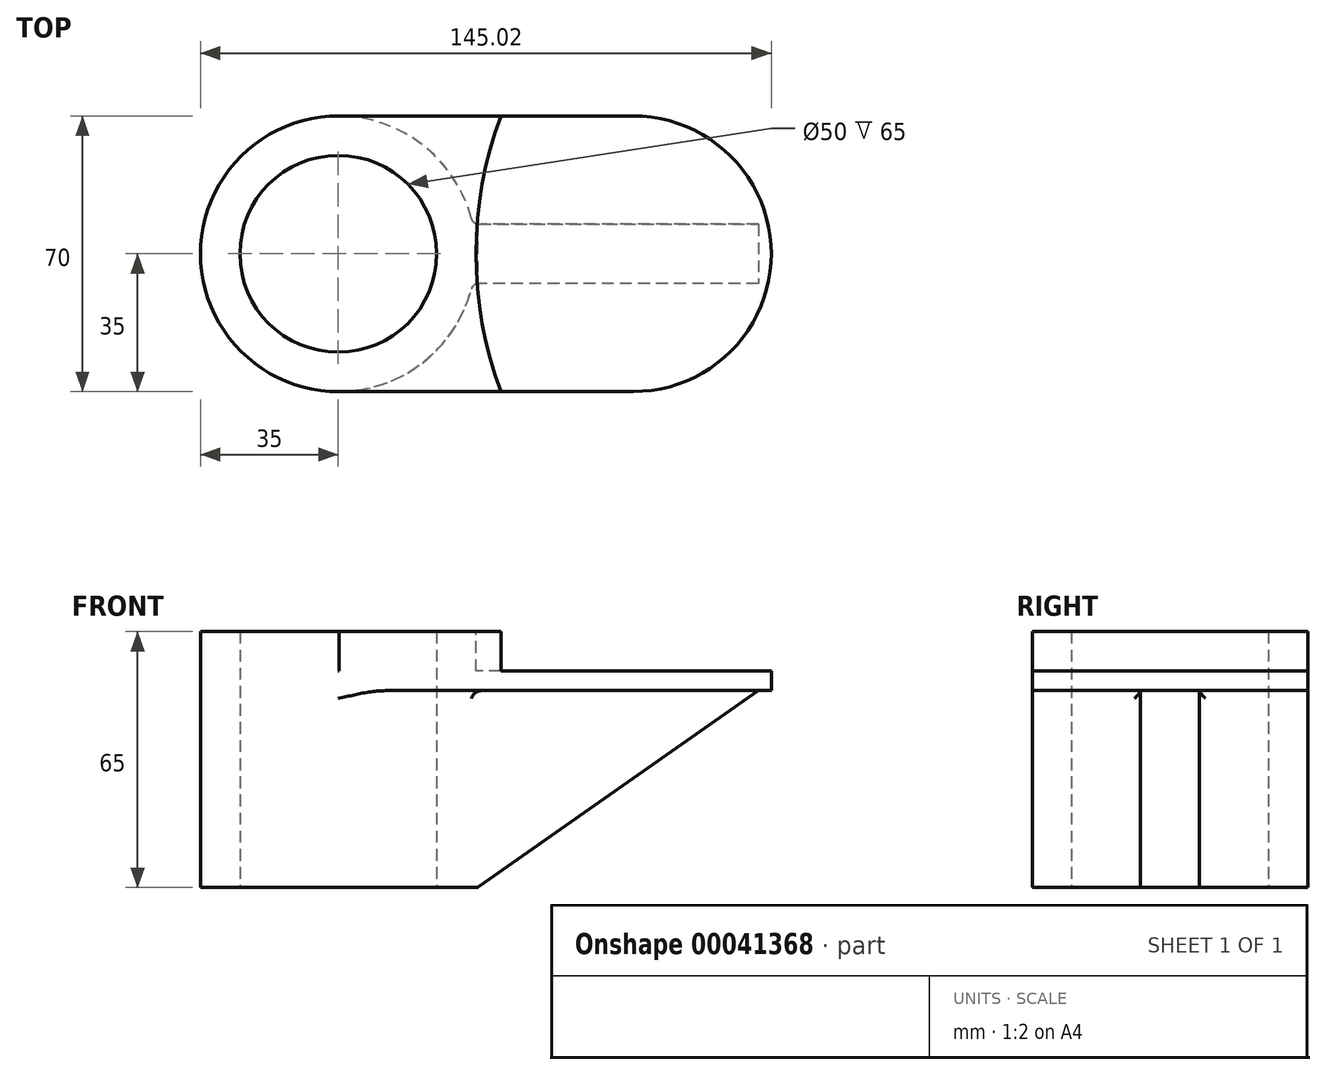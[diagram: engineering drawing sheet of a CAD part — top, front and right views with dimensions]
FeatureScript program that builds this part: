
annotation { "Feature Type Name" : "Feature", "Feature Type Description" : "" }
export const myFeature = defineFeature(function(context is Context, id is Id, definition is map)
    precondition{}
    {
        {
            var Q0;
            Q0=qCreatedBy(makeId("Top.planeOp"),FACE);
            var sketch = newSketch(context, id + "F0", { "sketchPlane" : qUnion([Q0])});
            skCircle(sketch, "E0", {"center": v(0, 0) * mm, "radius": 35 * mm});
            skSolve(sketch);
        }
        {
            var Q0;
            Q0=makeQuery(id+"F0.imprint","IMPRINT",FACE,{"disambiguationData":[TD([[makeQuery(id+"F0.imprint","IMPRINT",EDGE,{"derivedFrom":sQuery(id+"F0.wireOp",EDGE,"E0")}),1.0]])]});
            extrude(context, id + "F1", {"entities" : qUnion([Q0]), "depth" : 15 * mm, "hasSecondDirection" : true, "secondDirectionOppositeDirection" : true, "secondDirectionDepth" : 50 * mm});
        }
        {
            var Q0;
            Q0=qCreatedBy(makeId("Top.planeOp"),FACE);
            var sketch = newSketch(context, id + "F2", { "sketchPlane" : qUnion([Q0])});
            skLineSegment(sketch, "E1.rect.bottom", {"start": v(75, 35) * mm, "end": v(0, 35) * mm});
            skLineSegment(sketch, "E1.rect.top", {"start": v(75, -35) * mm, "end": v(0, -35) * mm});
            skLineSegment(sketch, "E1.rect.left", {"start": v(75, 35) * mm, "end": v(75, -35) * mm});
            skLineSegment(sketch, "E1.rect.right", {"start": v(0, 35) * mm, "end": v(0, -35) * mm});
            skPoint(sketch, "E1.rect.middle", {"position": v(37.5, 0) * mm});
            skSolve(sketch);
        }
        {
            var Q0;
            Q0=qCreatedBy(makeId("Top.planeOp"),FACE);
            var sketch = newSketch(context, id + "F3", { "sketchPlane" : qUnion([Q0])});
            skCircle(sketch, "E2", {"center": v(75.02, 0) * mm, "radius": 35 * mm});
            skSolve(sketch);
        }
        {
            var Q0;
            Q0=makeQuery(id+"F3.imprint","IMPRINT",FACE,{"disambiguationData":[TD([[makeQuery(id+"F3.imprint","IMPRINT",EDGE,{"derivedFrom":sQuery(id+"F3.wireOp",EDGE,"E2")}),1.0]])]});
            var Q1;
            Q1=makeQuery(id+"F2.imprint","IMPRINT",FACE,{"disambiguationData":[TD([[makeQuery(id+"F2.imprint","IMPRINT",EDGE,{"derivedFrom":sQuery(id+"F2.wireOp",EDGE,"E1.rect.bottom")}),1.0]])]});
            extrude(context, id + "F4", {"entities" : qUnion([Q0, Q1]), "operationType" : NewBodyOperationType.ADD, "depth" : 5 * mm});
        }
        {
            var Q0;
            Q0=makeQuery(id+"F4.boolean.opBoolean","MERGE",FACE,{"derivedFrom":[makeQuery(id+"F4.opExtrude","CAP_FACE",FACE,{"disambiguationData":[OSD([sQuery(id+"F2.wireOp",EDGE,"E1.rect.bottom"),sQuery(id+"F2.wireOp",EDGE,"E1.rect.top"),sQuery(id+"F2.wireOp",EDGE,"E1.rect.left"),sQuery(id+"F2.wireOp",EDGE,"E1.rect.right")])],"isStart":false}),makeQuery(id+"F4.opExtrude","CAP_FACE",FACE,{"disambiguationData":[OSD([sQuery(id+"F3.wireOp",EDGE,"E2")])],"isStart":false})]});
            var sketch = newSketch(context, id + "F5", { "sketchPlane" : qUnion([Q0])});
            skLineSegment(sketch, "E3.rect.bottom", {"start": v(57.08, -35) * mm, "end": v(0.17, -35) * mm});
            skLineSegment(sketch, "E3.rect.top", {"start": v(57.08, 35) * mm, "end": v(0.17, 35) * mm});
            skLineSegment(sketch, "E3.rect.left", {"start": v(57.08, -35) * mm, "end": v(57.08, 35) * mm});
            skLineSegment(sketch, "E3.rect.right", {"start": v(0.17, -35) * mm, "end": v(0.17, 35) * mm});
            skPoint(sketch, "E3.rect.middle", {"position": v(28.62, 0) * mm});
            skSolve(sketch);
        }
        {
            var Q0;
            Q0 = qSketchRegion(id + "F5", true);
            extrude(context, id + "F6", {"entities" : qUnion([Q0]), "operationType" : NewBodyOperationType.ADD, "depth" : 10 * mm});
        }
        {
            var Q0;
            Q0=makeQuery(id+"F6.boolean.opBoolean","MERGE",FACE,{"derivedFrom":[makeQuery(id+"F1.opExtrude","CAP_FACE",FACE,{"disambiguationData":[OSD([sQuery(id+"F0.wireOp",EDGE,"E0")])],"isStart":false}),makeQuery(id+"F6.opExtrude","CAP_FACE",FACE,{"disambiguationData":[OSD([sQuery(id+"F5.wireOp",EDGE,"E3.rect.bottom"),sQuery(id+"F5.wireOp",EDGE,"E3.rect.top"),sQuery(id+"F5.wireOp",EDGE,"E3.rect.left"),sQuery(id+"F5.wireOp",EDGE,"E3.rect.right")])],"isStart":false})]});
            var sketch = newSketch(context, id + "F7", { "sketchPlane" : qUnion([Q0])});
            skCircle(sketch, "E4", {"center": v(135, 0) * mm, "radius": 100 * mm});
            skSolve(sketch);
        }
        {
            var Q0;
            {var subQ3=makeQuery(id+"F6.opExtrude","CAP_EDGE",EDGE,{"disambiguationData":[OSD([sQuery(id+"F5.wireOp",EDGE,"E3.rect.left")])],"isStart":false});Q0=makeQuery(id+"F7.imprint","IMPRINT",FACE,{"disambiguationData":[TD([[makeQuery(id+"F7.imprint","IMPRINT",EDGE,{"derivedFrom":subQ3}),1.0]])]});}
            extrude(context, id + "F8", {"entities" : qUnion([Q0]), "operationType" : NewBodyOperationType.REMOVE, "oppositeDirection" : true, "depth" : 10 * mm});
        }
        {
            var Q0;
            Q0=makeQuery(id+"F3.imprint","IMPRINT",FACE,{"disambiguationData":[TD([[makeQuery(id+"F3.imprint","IMPRINT",EDGE,{"derivedFrom":sQuery(id+"F3.wireOp",EDGE,"E2")}),1.0]])]});
            var sketch = newSketch(context, id + "F9", { "sketchPlane" : qUnion([Q0])});
            skLineSegment(sketch, "E5.rect.bottom", {"start": v(108.34, 7.5) * mm, "end": v(8.34, 7.5) * mm});
            skLineSegment(sketch, "E5.rect.top", {"start": v(108.34, -7.5) * mm, "end": v(8.34, -7.5) * mm});
            skLineSegment(sketch, "E5.rect.left", {"start": v(108.34, 7.5) * mm, "end": v(108.34, -7.5) * mm});
            skLineSegment(sketch, "E5.rect.right", {"start": v(8.34, 7.5) * mm, "end": v(8.34, -7.5) * mm});
            skPoint(sketch, "E5.rect.middle", {"position": v(58.34, 0) * mm});
            skSolve(sketch);
        }
        {
            var Q0;
            Q0 = qSketchRegion(id + "F9", true);
            extrude(context, id + "F10", {"entities" : qUnion([Q0]), "operationType" : NewBodyOperationType.ADD, "oppositeDirection" : true, "depth" : 50 * mm});
        }
        {
            var Q0;
            Q0=makeQuery(id+"F10.opExtrude","CAP_EDGE",EDGE,{"disambiguationData":[OSD([sQuery(id+"F9.wireOp",EDGE,"E5.rect.left")])],"isStart":false});
            chamfer(context, id + "F11", {"entities" : qUnion([Q0]), "chamferType" : ChamferType.OFFSET_ANGLE, "width" : 73 * mm, "oppositeDirection" : false, "angle" : 35 * degree, "tangentPropagation" : true});
        }
        {
            var Q0;
            Q0=makeQuery(id+"F10.boolean.opBoolean","MERGE",FACE,{"derivedFrom":[makeQuery(id+"F1.opExtrude","CAP_FACE",FACE,{"disambiguationData":[OSD([sQuery(id+"F0.wireOp",EDGE,"E0")])],"isStart":true}),makeQuery(id+"F10.opExtrude","CAP_FACE",FACE,{"disambiguationData":[OSD([sQuery(id+"F9.wireOp",EDGE,"E5.rect.bottom"),sQuery(id+"F9.wireOp",EDGE,"E5.rect.top"),sQuery(id+"F9.wireOp",EDGE,"E5.rect.left"),sQuery(id+"F9.wireOp",EDGE,"E5.rect.right")])],"isStart":false})]});
            var sketch = newSketch(context, id + "F12", { "sketchPlane" : qUnion([Q0])});
            skCircle(sketch, "E6", {"center": v(0, 0) * mm, "radius": 25 * mm});
            skSolve(sketch);
        }
        {
            var Q0;
            Q0=makeQuery(id+"F12.imprint","IMPRINT",FACE,{"disambiguationData":[TD([[makeQuery(id+"F12.imprint","IMPRINT",EDGE,{"derivedFrom":sQuery(id+"F12.wireOp",EDGE,"E6")}),1.0]])]});
            extrude(context, id + "F13", {"entities" : qUnion([Q0]), "operationType" : NewBodyOperationType.REMOVE, "endBound" : BoundingType.THROUGH_ALL, "oppositeDirection" : true, "depth" : 25.4 * mm});
        }
        {
            var Q0;
            Q0=makeQuery(id+"F10.opExtrude","CAP_EDGE",EDGE,{"disambiguationData":[OSD([sQuery(id+"F9.wireOp",EDGE,"E5.rect.top")])],"isStart":true});
            var Q1;
            Q1=makeQuery(id+"F10.opExtrude","CAP_EDGE",EDGE,{"disambiguationData":[OSD([sQuery(id+"F9.wireOp",EDGE,"E5.rect.bottom")])],"isStart":true});
            var Q2;
            Q2=makeQuery(id+"F10.boolean.opBoolean","INTERSECT",EDGE,{"derivedFrom":[makeQuery(id+"F1.opExtrude","SWEPT_FACE",FACE,{"disambiguationData":[OSD([sQuery(id+"F0.wireOp",EDGE,"E0")])]}),makeQuery(id+"F10.opExtrude","SWEPT_FACE",FACE,{"disambiguationData":[OSD([sQuery(id+"F9.wireOp",EDGE,"E5.rect.top")])]})]});
            var Q3;
            Q3=makeQuery(id+"F10.boolean.opBoolean","INTERSECT",EDGE,{"derivedFrom":[makeQuery(id+"F1.opExtrude","SWEPT_FACE",FACE,{"disambiguationData":[OSD([sQuery(id+"F0.wireOp",EDGE,"E0")])]}),makeQuery(id+"F10.opExtrude","SWEPT_FACE",FACE,{"disambiguationData":[OSD([sQuery(id+"F9.wireOp",EDGE,"E5.rect.bottom")])]})]});
            var Q4;
            {var subQ0=makeQuery(id+"F1.opExtrude","SWEPT_FACE",FACE,{"disambiguationData":[OSD([sQuery(id+"F0.wireOp",EDGE,"E0")])]});var subQ1=sQuery(id+"F2.wireOp",EDGE,"E1.rect.top");var subQ2=makeQuery(id+"F4.opExtrude","CAP_FACE",FACE,{"disambiguationData":[OSD([sQuery(id+"F2.wireOp",EDGE,"E1.rect.bottom"),subQ1,sQuery(id+"F2.wireOp",EDGE,"E1.rect.left"),sQuery(id+"F2.wireOp",EDGE,"E1.rect.right")])],"isStart":true});var subQ3=makeQuery(id+"F4.opExtrude","CAP_FACE",FACE,{"disambiguationData":[OSD([sQuery(id+"F3.wireOp",EDGE,"E2")])],"isStart":true});Q4=makeQuery(id+"F10.boolean.opBoolean","SPLIT",EDGE,{"disambiguationData":[TD([makeQuery(id+"F4.opExtrude","SWEPT_FACE",FACE,{"disambiguationData":[OSD([subQ1])]})])],"derivedFrom":makeQuery(id+"F4.boolean.opBoolean","INTERSECT",EDGE,{"derivedFrom":[subQ0,subQ2,subQ3]})});}
            var Q5;
            {var subQ0=makeQuery(id+"F1.opExtrude","SWEPT_FACE",FACE,{"disambiguationData":[OSD([sQuery(id+"F0.wireOp",EDGE,"E0")])]});var subQ1=sQuery(id+"F2.wireOp",EDGE,"E1.rect.bottom");var subQ2=makeQuery(id+"F4.opExtrude","CAP_FACE",FACE,{"disambiguationData":[OSD([subQ1,sQuery(id+"F2.wireOp",EDGE,"E1.rect.top"),sQuery(id+"F2.wireOp",EDGE,"E1.rect.left"),sQuery(id+"F2.wireOp",EDGE,"E1.rect.right")])],"isStart":true});var subQ3=makeQuery(id+"F4.opExtrude","CAP_FACE",FACE,{"disambiguationData":[OSD([sQuery(id+"F3.wireOp",EDGE,"E2")])],"isStart":true});Q5=makeQuery(id+"F10.boolean.opBoolean","SPLIT",EDGE,{"disambiguationData":[TD([makeQuery(id+"F4.opExtrude","SWEPT_FACE",FACE,{"disambiguationData":[OSD([subQ1])]})])],"derivedFrom":makeQuery(id+"F4.boolean.opBoolean","INTERSECT",EDGE,{"derivedFrom":[subQ0,subQ2,subQ3]})});}
            fillet(context, id + "F14", {"entities" : qUnion([Q0, Q1, Q2, Q3, Q4, Q5]), "radius" : 2 * mm, "tangentPropagation" : true, "allowEdgeOverflow" : false});
        }
    });
